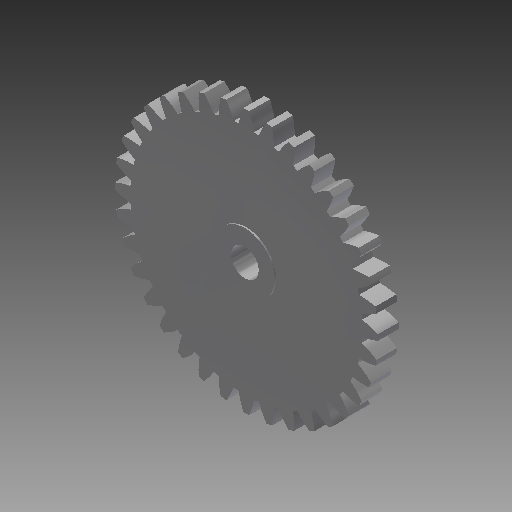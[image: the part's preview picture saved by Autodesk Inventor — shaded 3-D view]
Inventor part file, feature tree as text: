
AUTODESK INVENTOR PART (.ipt)
format: ipt  version: 2017 (Build 210142000, 142)  size: 298,496 bytes
history: native  units: mm (DEFAULTED — no unit token found)
features: sketch x4, extrude x3, plane x3, other x3
ambient origin geometry x8: Origin, YZ Plane, XZ Plane, XY Plane, X Axis, Y Axis, Z Axis, Center Point
bodies: Solid1 (feature_tree)
feature tree (13):
  extrude  "Extrusion1"  Depth=1.5mm TaperAngle=0.0deg
  plane  "Work Plane2"
  plane  "Work Plane8"
  plane  "Work Plane9"
  other  "Spur Gear"
  extrude  "Extrusion2"  Depth=10.0mm TaperAngle=0.0deg
  extrude  "Extrusion3"  Depth=0.872665mm TaperAngle=0.0deg
  sketch  "Sketch1"  dims[d0=19.0mm d1=1.5mm d2=0.0mm]
  sketch  "Sketch2"  dims[d3=18.0mm d4=10.0mm d5=0.0mm]
  other  "Srf1"
  sketch  "Sketch3"  dims[d16=11.5mm d17=0.0mm d34=0.872665mm]
  sketch  "Sketch4"  dims[d39=0.0mm d41=0.0mm d43=11.5mm d46=11.5mm d47=0.0mm d48=0.0mm d49=4.3mm d50=0.1mm d51=0.0mm d52=2.0mm d53=0.1mm d54=0.0mm]
  other  "Pitch Diameter"
